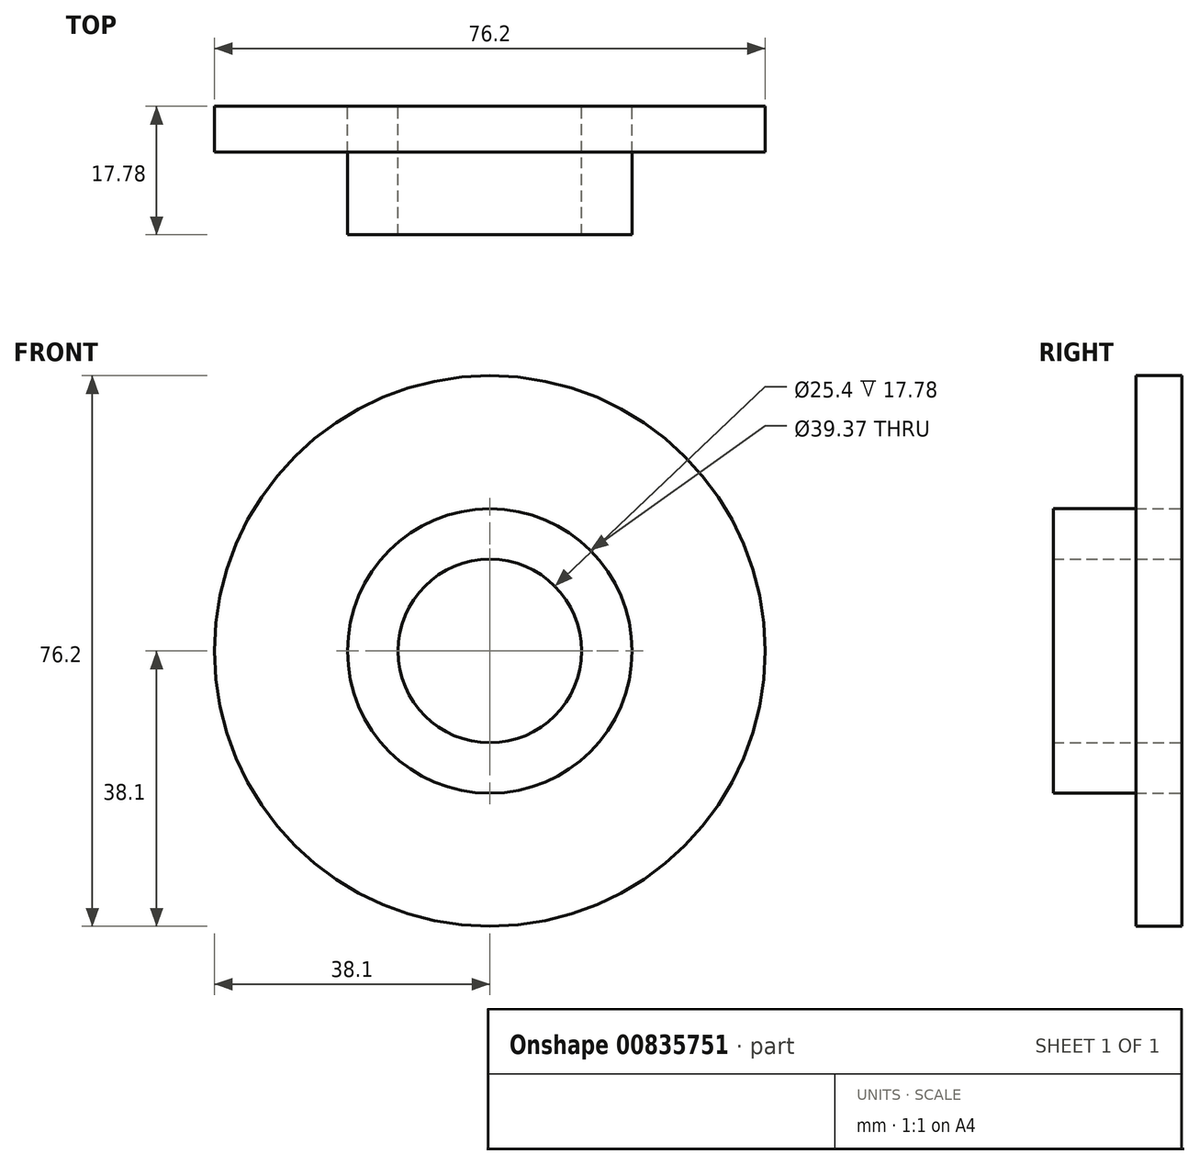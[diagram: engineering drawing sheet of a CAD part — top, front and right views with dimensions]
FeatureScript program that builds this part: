
annotation { "Feature Type Name" : "Feature", "Feature Type Description" : "" }
export const myFeature = defineFeature(function(context is Context, id is Id, definition is map)
    precondition{}
    {
        {
            var Q0;
            Q0=qCreatedBy(makeId("Front.planeOp"),FACE);
            var sketch = newSketch(context, id + "F0", { "sketchPlane" : qUnion([Q0])});
            skCircle(sketch, "E0", {"center": v(0, 0) * mm, "radius": 38.1 * mm});
            skCircle(sketch, "E1", {"center": v(0, 0) * mm, "radius": 19.69 * mm});
            skCircle(sketch, "E2", {"center": v(0, 0) * mm, "radius": 12.7 * mm});
            skSolve(sketch);
        }
        {
            var Q0;
            Q0=makeQuery(id+"F0.imprint","IMPRINT",FACE,{"disambiguationData":[TD([[makeQuery(id+"F0.imprint","IMPRINT",EDGE,{"derivedFrom":sQuery(id+"F0.wireOp",EDGE,"E0")}),1.0]])]});
            extrude(context, id + "F1", {"entities" : qUnion([Q0]), "depth" : 6.35 * mm, "offsetDistance" : 25.4 * mm});
        }
        {
            var Q0;
            Q0=makeQuery(id+"F0.imprint","IMPRINT",FACE,{"disambiguationData":[TD([[makeQuery(id+"F0.imprint","IMPRINT",EDGE,{"derivedFrom":sQuery(id+"F0.wireOp",EDGE,"E1")}),1.0]])]});
            var Q1;
            Q1=sQuery(id+"F0.wireOp",EDGE,"E2");
            var Q2;
            Q2=sQuery(id+"F0.wireOp",EDGE,"E1");
            extrude(context, id + "F2", {"entities" : qUnion([Q0]), "surfaceEntities" : qUnion([Q1, Q2]), "depth" : 17.78 * mm, "offsetDistance" : 25.4 * mm});
        }
    });
